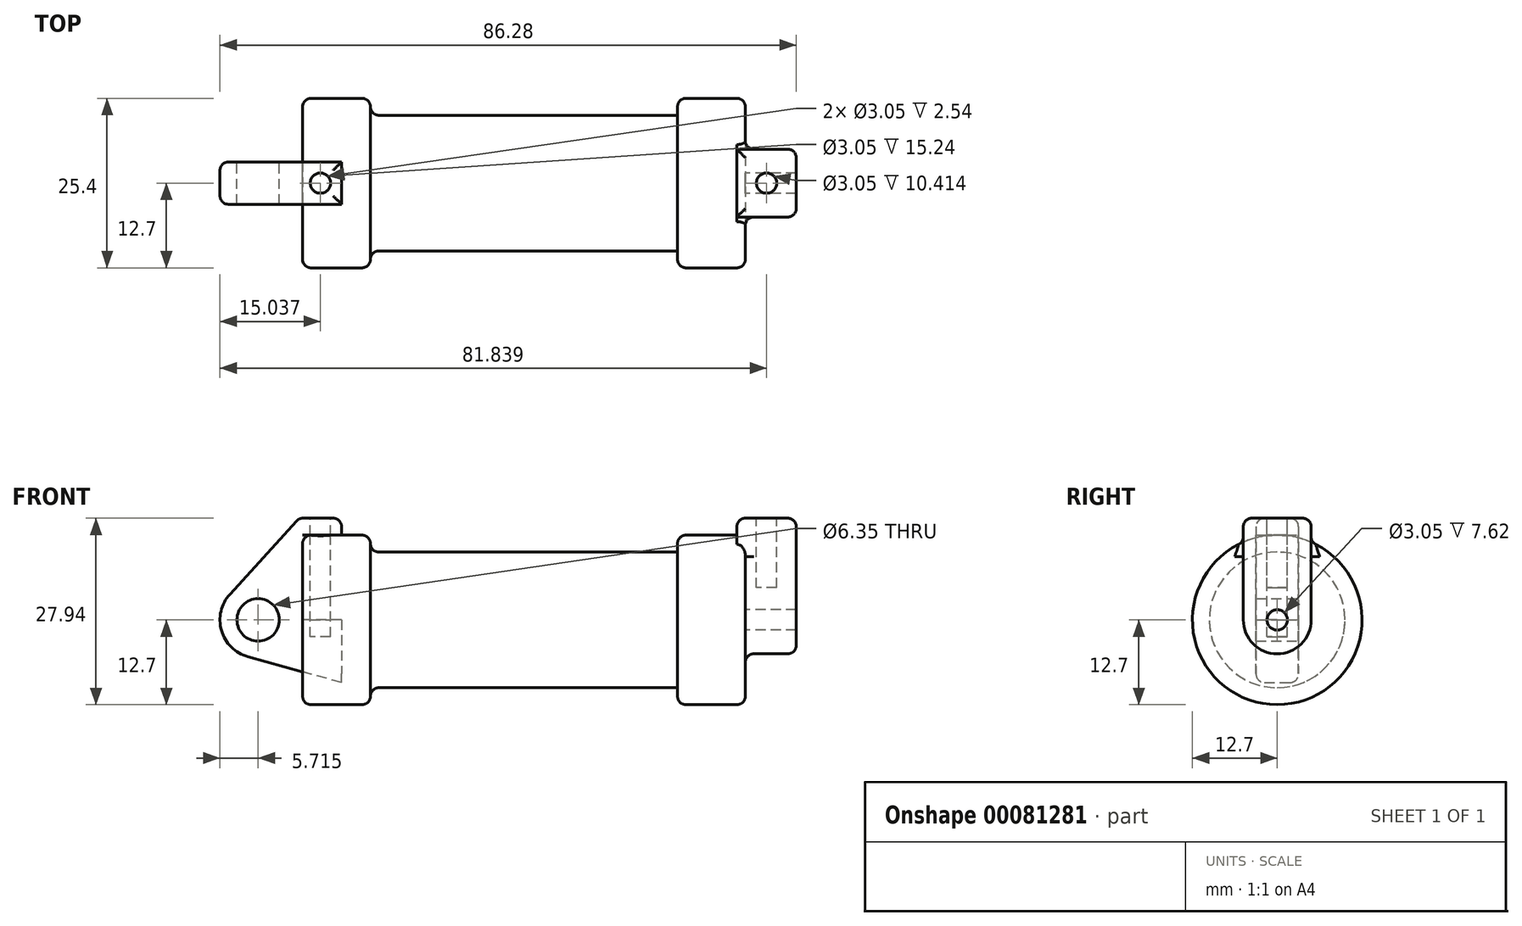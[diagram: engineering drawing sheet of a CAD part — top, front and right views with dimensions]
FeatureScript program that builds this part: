
annotation { "Feature Type Name" : "Feature", "Feature Type Description" : "" }
export const myFeature = defineFeature(function(context is Context, id is Id, definition is map)
    precondition{}
    {
        {
            var Q0;
            Q0=qCreatedBy(makeId("Front.planeOp"),FACE);
            var sketch = newSketch(context, id + "F0", { "sketchPlane" : qUnion([Q0])});
            skLineSegment(sketch, "E0", {"start": v(0, 0) * mm, "end": v(0, 12.7) * mm});
            skLineSegment(sketch, "E1", {"start": v(0, 12.7) * mm, "end": v(10.16, 12.7) * mm});
            skLineSegment(sketch, "E2", {"start": v(10.16, 12.7) * mm, "end": v(10.16, 10.16) * mm});
            skLineSegment(sketch, "E3", {"start": v(10.16, 10.16) * mm, "end": v(56.13, 10.16) * mm});
            skLineSegment(sketch, "E4", {"start": v(56.13, 10.16) * mm, "end": v(56.13, 12.7) * mm});
            skLineSegment(sketch, "E5", {"start": v(56.13, 12.7) * mm, "end": v(66.3, 12.7) * mm});
            skLineSegment(sketch, "E6", {"start": v(66.3, 12.7) * mm, "end": v(66.3, 0) * mm});
            skLineSegment(sketch, "E7", {"start": v(66.3, 0) * mm, "end": v(0, 0) * mm});
            skLineSegment(sketch, "E8", {"start": v(5.84, 15.24) * mm, "end": v(-0.5, 15.24) * mm});
            skLineSegment(sketch, "E9", {"start": v(-0.5, 15.24) * mm, "end": v(-10.88, 3.85) * mm});
            skLineSegment(sketch, "E10", {"start": v(0, 0) * mm, "end": v(-6.65, 0) * mm});
            skCircle(sketch, "E11", {"center": v(-6.65, 0) * mm, "radius": 5.72 * mm});
            skCircle(sketch, "E12", {"center": v(-6.65, 0) * mm, "radius": 3.18 * mm});
            skLineSegment(sketch, "E13", {"start": v(5.84, 15.24) * mm, "end": v(5.84, -9.4) * mm});
            skLineSegment(sketch, "E14", {"start": v(5.84, -9.4) * mm, "end": v(-8.18, -5.5) * mm});
            skSolve(sketch);
        }
        {
            var Q0;
            {var subQ0=sQuery(id+"F0.wireOp",EDGE,"E0");Q0=makeQuery(id+"F0.imprint","IMPRINT",FACE,{"disambiguationData":[TD([[makeQuery(id+"F0.imprint","IMPRINT",EDGE,{"derivedFrom":subQ0}),-1.0]])]});}
            var Q1;
            {var subQ0=sQuery(id+"F0.wireOp",EDGE,"E2");Q1=makeQuery(id+"F0.imprint","IMPRINT",FACE,{"disambiguationData":[TD([[makeQuery(id+"F0.imprint","IMPRINT",EDGE,{"derivedFrom":subQ0}),-1.0]])]});}
            var Q2;
            Q2=sQuery(id+"F0.wireOp",EDGE,"E7");
            revolve(context, id + "F1", {"entities" : qUnion([Q0, Q1]), "axis" : qUnion([Q2]), "revolveType" : RevolveType.FULL});
        }
        {
            var Q0;
            {var subQ3=sQuery(id+"F0.wireOp",EDGE,"E0");Q0=makeQuery(id+"F0.imprint","IMPRINT",FACE,{"disambiguationData":[TD([[makeQuery(id+"F0.imprint","IMPRINT",EDGE,{"derivedFrom":subQ3}),1.0]])]});}
            var Q1;
            {var subQ0=sQuery(id+"F0.wireOp",EDGE,"E14");Q1=makeQuery(id+"F0.imprint","IMPRINT",FACE,{"disambiguationData":[TD([[makeQuery(id+"F0.imprint","IMPRINT",EDGE,{"derivedFrom":subQ0}),-1.0]])]});}
            var Q2;
            {var subQ4=sQuery(id+"F0.wireOp",EDGE,"E12");Q2=makeQuery(id+"F0.imprint","IMPRINT",FACE,{"disambiguationData":[TD([[makeQuery(id+"F0.imprint","IMPRINT",EDGE,{"derivedFrom":subQ4}),-1.0]])]});}
            extrude(context, id + "F2", {"entities" : qUnion([Q0, Q1, Q2]), "endBound" : BoundingType.SYMMETRIC, "depth" : 6.35 * mm});
        }
        {
            var Q0;
            Q0=makeQuery(id+"F1.opRevolve","SWEPT_FACE",FACE,{"disambiguationData":[OSD([sQuery(id+"F0.wireOp",EDGE,"E6")])]});
            var sketch = newSketch(context, id + "F3", { "sketchPlane" : qUnion([Q0])});
            skCircle(sketch, "E15", {"center": v(0, 0) * mm, "radius": 1.52 * mm});
            skCircle(sketch, "E16", {"center": v(0, 0) * mm, "radius": 5.08 * mm});
            skLineSegment(sketch, "E17", {"start": v(-5.08, 0) * mm, "end": v(-5.08, 15.24) * mm});
            skLineSegment(sketch, "E18", {"start": v(5.08, 0) * mm, "end": v(5.08, 15.24) * mm});
            skLineSegment(sketch, "E19", {"start": v(5.08, 15.24) * mm, "end": v(-5.08, 15.24) * mm});
            skSolve(sketch);
        }
        {
            var Q0;
            Q0=makeQuery(id+"F3.imprint","IMPRINT",FACE,{"disambiguationData":[TD([[makeQuery(id+"F3.imprint","IMPRINT",EDGE,{"derivedFrom":sQuery(id+"F3.wireOp",EDGE,"E15")}),-1.0]])]});
            var Q1;
            {var subQ0=sQuery(id+"F3.wireOp",EDGE,"E17");var subQ1=sQuery(id+"F3.wireOp",EDGE,"E16");var subQ2=makeQuery(id+"F3.imprint","INTERSECT",VERTEX,{"derivedFrom":[subQ1,subQ0]});Q1=makeQuery(id+"F3.imprint","IMPRINT",FACE,{"disambiguationData":[TD([[makeQuery(id+"F3.imprint","IMPRINT",EDGE,{"disambiguationData":[TD([[subQ2,1.0]])],"derivedFrom":subQ1}),-1.0]])]});}
            var Q2;
            {var subQ0=sQuery(id+"F3.wireOp",EDGE,"E19");Q2=makeQuery(id+"F3.imprint","IMPRINT",FACE,{"disambiguationData":[TD([[makeQuery(id+"F3.imprint","IMPRINT",EDGE,{"derivedFrom":subQ0}),1.0]])]});}
            extrude(context, id + "F4", {"entities" : qUnion([Q0, Q1, Q2]), "operationType" : NewBodyOperationType.ADD, "depth" : 7.62 * mm, "hasSecondDirection" : true, "secondDirectionOppositeDirection" : true, "secondDirectionDepth" : 1.27 * mm});
        }
        {
            var Q0;
            Q0=makeQuery(id+"F4.boolean.opBoolean","SPLIT",FACE,{"disambiguationData":[TD([makeQuery(id+"F4.opExtrude","SWEPT_FACE",FACE,{"disambiguationData":[OSD([sQuery(id+"F3.wireOp",EDGE,"E15")])]})])],"derivedFrom":makeQuery(id+"F1.opRevolve","SWEPT_FACE",FACE,{"disambiguationData":[OSD([sQuery(id+"F0.wireOp",EDGE,"E6")])]})});
            var sketch = newSketch(context, id + "F5", { "sketchPlane" : qUnion([Q0])});
            skCircle(sketch, "E20", {"center": v(0, 0) * mm, "radius": 1.52 * mm});
            skSolve(sketch);
        }
        {
            var Q0;
            Q0=sQuery(id+"F5.wireOp",EDGE,"E20");
            extrude(context, id + "F6", {"bodyType" : ToolBodyType.SURFACE, "surfaceEntities" : qUnion([Q0]), "oppositeDirection" : true, "depth" : 56.14 * mm});
        }
        {
            var Q0;
            Q0=makeQuery(id+"F1.opRevolve","SWEPT_EDGE",EDGE,{"disambiguationData":[OSD([sQuery(id+"F0.wireOp",EDGE,"E4"),sQuery(id+"F0.wireOp",EDGE,"E5")])]});
            var Q1;
            Q1=makeQuery(id+"F1.opRevolve","SWEPT_EDGE",EDGE,{"disambiguationData":[OSD([sQuery(id+"F0.wireOp",EDGE,"E5"),sQuery(id+"F0.wireOp",EDGE,"E6")])]});
            var Q2;
            Q2=makeQuery(id+"F1.opRevolve","SWEPT_EDGE",EDGE,{"disambiguationData":[OSD([sQuery(id+"F0.wireOp",EDGE,"E1"),sQuery(id+"F0.wireOp",EDGE,"E2")])]});
            var Q3;
            Q3=makeQuery(id+"F1.opRevolve","SWEPT_EDGE",EDGE,{"disambiguationData":[OSD([sQuery(id+"F0.wireOp",EDGE,"E2"),sQuery(id+"F0.wireOp",EDGE,"E3")])]});
            var Q4;
            Q4=makeQuery(id+"F1.opRevolve","SWEPT_EDGE",EDGE,{"disambiguationData":[OSD([sQuery(id+"F0.wireOp",EDGE,"E0"),sQuery(id+"F0.wireOp",EDGE,"E1")])]});
            fillet(context, id + "F7", {"entities" : qUnion([Q0, Q1, Q2, Q3, Q4]), "radius" : 1.27 * mm, "tangentPropagation" : true, "allowEdgeOverflow" : false});
        }
        {
            var Q0;
            Q0=makeQuery(id+"F2.opExtrude","SWEPT_FACE",FACE,{"disambiguationData":[OSD([sQuery(id+"F0.wireOp",EDGE,"E8")])]});
            var sketch = newSketch(context, id + "F8", { "sketchPlane" : qUnion([Q0])});
            skCircle(sketch, "E21", {"center": v(2.67, 0) * mm, "radius": 1.52 * mm});
            skSolve(sketch);
        }
        {
            var Q0;
            Q0 = qSketchRegion(id + "F8", true);
            extrude(context, id + "F9", {"entities" : qUnion([Q0]), "operationType" : NewBodyOperationType.REMOVE, "oppositeDirection" : true, "depth" : 17.78 * mm});
        }
        {
            var Q0;
            Q0=makeQuery(id+"F4.opExtrude","SWEPT_FACE",FACE,{"disambiguationData":[OSD([sQuery(id+"F3.wireOp",EDGE,"E19")])]});
            var sketch = newSketch(context, id + "F10", { "sketchPlane" : qUnion([Q0])});
            skCircle(sketch, "E22", {"center": v(69.47, 0) * mm, "radius": 1.52 * mm});
            skSolve(sketch);
        }
        {
            var Q0;
            Q0 = qSketchRegion(id + "F10", true);
            extrude(context, id + "F11", {"entities" : qUnion([Q0]), "operationType" : NewBodyOperationType.REMOVE, "oppositeDirection" : true, "depth" : 10.4 * mm});
        }
        {
            var Q0;
            Q0=makeQuery(id+"F2.opExtrude","CAP_EDGE",EDGE,{"disambiguationData":[OSD([sQuery(id+"F0.wireOp",EDGE,"E9")])],"isStart":false});
            var Q1;
            Q1=makeQuery(id+"F2.opExtrude","CAP_EDGE",EDGE,{"disambiguationData":[OSD([sQuery(id+"F0.wireOp",EDGE,"E9")])],"isStart":true});
            var Q2;
            Q2=makeQuery(id+"F2.opExtrude","SWEPT_EDGE",EDGE,{"disambiguationData":[OSD([sQuery(id+"F0.wireOp",EDGE,"E8"),sQuery(id+"F0.wireOp",EDGE,"E9")])]});
            var Q3;
            Q3=makeQuery(id+"F2.opExtrude","CAP_EDGE",EDGE,{"disambiguationData":[OSD([sQuery(id+"F0.wireOp",EDGE,"E8")])],"isStart":false});
            var Q4;
            Q4=makeQuery(id+"F2.opExtrude","CAP_EDGE",EDGE,{"disambiguationData":[OSD([sQuery(id+"F0.wireOp",EDGE,"E8")])],"isStart":true});
            var Q5;
            Q5=makeQuery(id+"F2.opExtrude","SWEPT_EDGE",EDGE,{"disambiguationData":[OSD([sQuery(id+"F0.wireOp",EDGE,"E8"),sQuery(id+"F0.wireOp",EDGE,"E13")])]});
            var Q6;
            Q6=makeQuery(id+"F4.opExtrude","SWEPT_EDGE",EDGE,{"disambiguationData":[OSD([sQuery(id+"F3.wireOp",EDGE,"E17"),sQuery(id+"F3.wireOp",EDGE,"E19")])]});
            var Q7;
            Q7=makeQuery(id+"F4.opExtrude","CAP_EDGE",EDGE,{"disambiguationData":[OSD([sQuery(id+"F3.wireOp",EDGE,"E19")])],"isStart":false});
            var Q8;
            Q8=makeQuery(id+"F4.opExtrude","SWEPT_EDGE",EDGE,{"disambiguationData":[OSD([sQuery(id+"F3.wireOp",EDGE,"E18"),sQuery(id+"F3.wireOp",EDGE,"E19")])]});
            var Q9;
            Q9=makeQuery(id+"F4.opExtrude","CAP_EDGE",EDGE,{"disambiguationData":[OSD([sQuery(id+"F3.wireOp",EDGE,"E19")])],"isStart":true});
            var Q10;
            Q10=makeQuery(id+"F4.opExtrude","CAP_EDGE",EDGE,{"disambiguationData":[OSD([sQuery(id+"F3.wireOp",EDGE,"E17")])],"isStart":false});
            var Q11;
            Q11=makeQuery(id+"F4.boolean.opBoolean","INTERSECT",EDGE,{"derivedFrom":[makeQuery(id+"F1.opRevolve","SWEPT_FACE",FACE,{"disambiguationData":[OSD([sQuery(id+"F0.wireOp",EDGE,"E6")])]}),makeQuery(id+"F4.opExtrude","SWEPT_FACE",FACE,{"disambiguationData":[OSD([sQuery(id+"F3.wireOp",EDGE,"E17")])]})]});
            fillet(context, id + "F12", {"entities" : qUnion([Q0, Q1, Q2, Q3, Q4, Q5, Q6, Q7, Q8, Q9, Q10, Q11]), "radius" : 1.27 * mm, "tangentPropagation" : true, "allowEdgeOverflow" : false});
        }
    });
